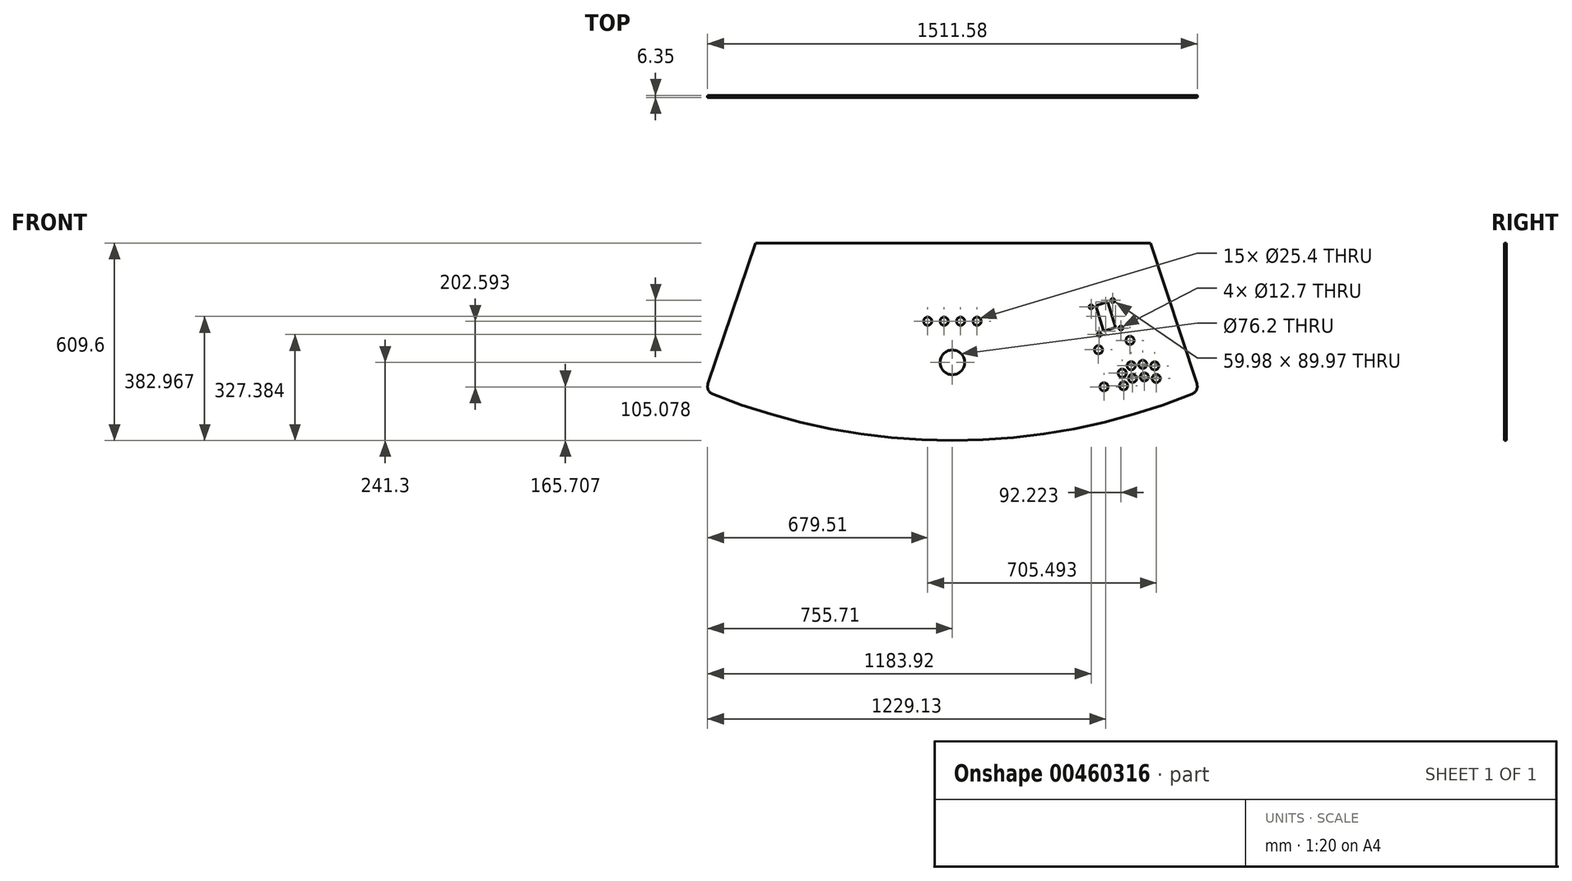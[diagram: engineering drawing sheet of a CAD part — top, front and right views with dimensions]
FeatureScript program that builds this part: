
annotation { "Feature Type Name" : "Feature", "Feature Type Description" : "" }
export const myFeature = defineFeature(function(context is Context, id is Id, definition is map)
    precondition{}
    {
        {
            var Q0;
            Q0=qCreatedBy(makeId("Front.planeOp"),FACE);
            var sketch = newSketch(context, id + "F0", { "sketchPlane" : qUnion([Q0])});
            skLineSegment(sketch, "E0.bottom", {"start": v(-607.8, 0) * mm, "end": v(611.4, 0) * mm});
            skLineSegment(sketch, "E1", {"start": v(-607.8, 0) * mm, "end": v(-754.38, -434.61) * mm});
            skLineSegment(sketch, "E2", {"start": v(611.4, 0) * mm, "end": v(754.6, -434.72) * mm});
            skArc(sketch, "E3", {"start": v(-739.8, -466.3) * mm, "mid": v(0.09, -609.6) * mm, "end": v(739.96, -466.23) * mm});
            skPoint(sketch, "E4.visualSharp", {"position": v(-762, -457.2) * mm});
            skArc(sketch, "E4.filletArc", {"start": v(-754.38, -434.61) * mm, "mid": v(-753.39, -453.35) * mm, "end": v(-739.8, -466.3) * mm});
            skPoint(sketch, "E5.visualSharp", {"position": v(762, -457.2) * mm});
            skArc(sketch, "E5.filletArc", {"start": v(739.96, -466.23) * mm, "mid": v(753.5, -453.37) * mm, "end": v(754.6, -434.72) * mm});
            skSolve(sketch);
        }
        {
            var Q0;
            Q0=qSketchRegion(id+"F0",true);
            extrude(context, id + "F1", {"entities" : qUnion([Q0]), "depth" : 6.35 * mm});
        }
        {
            var Q0;
            Q0=makeQuery(id+"F1.opExtrude","CAP_FACE",FACE,{"disambiguationData":[OSD([sQuery(id+"F0.wireOp",EDGE,"E0.bottom"),sQuery(id+"F0.wireOp",EDGE,"E1"),sQuery(id+"F0.wireOp",EDGE,"E2"),sQuery(id+"F0.wireOp",EDGE,"E3"),sQuery(id+"F0.wireOp",EDGE,"E4.filletArc"),sQuery(id+"F0.wireOp",EDGE,"E5.filletArc")])],"isStart":false});
            var sketch = newSketch(context, id + "F2", { "sketchPlane" : qUnion([Q0])});
            skCircle(sketch, "E6", {"center": v(0, 1371.6) * mm, "radius": 1981.2 * mm, "construction": true});
            skLineSegment(sketch, "E7", {"start": v(0, 1371.6) * mm, "end": v(-562.7, -528.01) * mm, "construction": true});
            skLineSegment(sketch, "E8", {"start": v(0, 1371.6) * mm, "end": v(-189.89, -600.48) * mm, "construction": true});
            skLineSegment(sketch, "E9", {"start": v(0, 1371.6) * mm, "end": v(189.89, -600.48) * mm, "construction": true});
            skLineSegment(sketch, "E10", {"start": v(0, 1371.6) * mm, "end": v(562.7, -528.01) * mm, "construction": true});
            skLineSegment(sketch, "E11", {"start": v(0, 1371.6) * mm, "end": v(-762, -457.2) * mm, "construction": true});
            skLineSegment(sketch, "E12", {"start": v(0, 1371.6) * mm, "end": v(762, -457.2) * mm, "construction": true});
            skLineSegment(sketch, "E13", {"start": v(0, 1371.6) * mm, "end": v(0, -609.6) * mm, "construction": true});
            skLineSegment(sketch, "E14.bottom", {"start": v(422.55, -417.2) * mm, "end": v(618.63, -359.12) * mm, "construction": true});
            skLineSegment(sketch, "E14.top", {"start": v(442.39, -484.18) * mm, "end": v(638.47, -426.1) * mm, "construction": true});
            skLineSegment(sketch, "E14.left", {"start": v(422.55, -417.2) * mm, "end": v(442.39, -484.18) * mm, "construction": true});
            skLineSegment(sketch, "E14.right", {"start": v(618.63, -359.12) * mm, "end": v(638.47, -426.1) * mm, "construction": true});
            skCircle(sketch, "E15", {"center": v(624.6, -379.26) * mm, "radius": 12.7 * mm});
            skCircle(sketch, "E16", {"center": v(629.3, -418.02) * mm, "radius": 12.7 * mm});
            skCircle(sketch, "E17", {"center": v(587.73, -374.53) * mm, "radius": 12.7 * mm});
            skCircle(sketch, "E18", {"center": v(592.43, -413.3) * mm, "radius": 12.7 * mm});
            skCircle(sketch, "E19", {"center": v(551.99, -378.86) * mm, "radius": 12.7 * mm});
            skCircle(sketch, "E20", {"center": v(556.21, -417.76) * mm, "radius": 12.7 * mm});
            skCircle(sketch, "E21", {"center": v(524.32, -401.66) * mm, "radius": 12.7 * mm});
            skCircle(sketch, "E22", {"center": v(528.55, -440.56) * mm, "radius": 12.7 * mm});
            skCircle(sketch, "E23", {"center": v(468, -443.9) * mm, "radius": 12.7 * mm});
            skCircle(sketch, "E24", {"center": v(450.86, -329.34) * mm, "radius": 12.7 * mm});
            skCircle(sketch, "E25", {"center": v(548.28, -300.49) * mm, "radius": 12.7 * mm});
            skLineSegment(sketch, "E26", {"start": v(443.43, -192.47) * mm, "end": v(479.96, -181.65) * mm});
            skLineSegment(sketch, "E27", {"start": v(479.96, -181.65) * mm, "end": v(503.4, -260.8) * mm});
            skLineSegment(sketch, "E28", {"start": v(503.4, -260.8) * mm, "end": v(466.88, -271.62) * mm});
            skLineSegment(sketch, "E29", {"start": v(466.88, -271.62) * mm, "end": v(443.43, -192.47) * mm});
            skCircle(sketch, "E30", {"center": v(453.46, -282.22) * mm, "radius": 6.35 * mm});
            skCircle(sketch, "E31", {"center": v(520.43, -262.38) * mm, "radius": 6.35 * mm});
            skCircle(sketch, "E32", {"center": v(428.2, -196.98) * mm, "radius": 6.35 * mm});
            skCircle(sketch, "E33", {"center": v(495.18, -177.14) * mm, "radius": 6.35 * mm});
            skSolve(sketch);
        }
        {
            var Q0;
            Q0=qSketchRegion(id+"F2",true);
            extrude(context, id + "F3", {"entities" : qUnion([Q0]), "operationType" : NewBodyOperationType.REMOVE, "endBound" : BoundingType.THROUGH_ALL, "oppositeDirection" : true, "depth" : 25.4 * mm});
        }
        {
            var Q0;
            Q0=qCreatedBy(makeId("Top.planeOp"),FACE);
            cPlane(context, id + "F4", {"entities" : qUnion([Q0]), "cplaneType" : CPlaneType.OFFSET, "offset" : 1371.6 * mm, "width" : 152.4 * mm, "height" : 152.4 * mm});
        }
        {
            var Q0;
            Q0=qCreatedBy(id+"F4.planeOp",FACE);
            var sketch = newSketch(context, id + "F5", { "sketchPlane" : qUnion([Q0])});
            skLineSegment(sketch, "E34", {"start": v(0.09, -217.76) * mm, "end": v(0.09, 314.08) * mm, "construction": true});
            skSolve(sketch);
        }
        {
            var Q0;
            Q0=makeQuery(id+"F1.opExtrude","CAP_FACE",FACE,{"disambiguationData":[OSD([sQuery(id+"F0.wireOp",EDGE,"E0.bottom"),sQuery(id+"F0.wireOp",EDGE,"E1"),sQuery(id+"F0.wireOp",EDGE,"E2"),sQuery(id+"F0.wireOp",EDGE,"E3"),sQuery(id+"F0.wireOp",EDGE,"E4.filletArc"),sQuery(id+"F0.wireOp",EDGE,"E5.filletArc")])],"isStart":false});
            var sketch = newSketch(context, id + "F6", { "sketchPlane" : qUnion([Q0])});
            skLineSegment(sketch, "E35", {"start": v(0, 0) * mm, "end": v(0, -609.6) * mm, "construction": true});
            skCircle(sketch, "E36", {"center": v(0, -368.3) * mm, "radius": 38.1 * mm});
            skLineSegment(sketch, "E37", {"start": v(-99.18, -254) * mm, "end": v(154.82, -254) * mm, "construction": true});
            skCircle(sketch, "E38", {"center": v(-76.2, -241.3) * mm, "radius": 12.7 * mm});
            skCircle(sketch, "E39.1.0.0", {"center": v(-25.4, -241.3) * mm, "radius": 12.7 * mm});
            skCircle(sketch, "E39.2.0.0", {"center": v(25.4, -241.3) * mm, "radius": 12.7 * mm});
            skCircle(sketch, "E39.3.0.0", {"center": v(76.2, -241.3) * mm, "radius": 12.7 * mm});
            skLineSegment(sketch, "E39.direction1", {"start": v(-76.2, -241.3) * mm, "end": v(-25.4, -241.3) * mm, "construction": true});
            skSolve(sketch);
        }
        {
            var Q0;
            Q0=qSketchRegion(id+"F6",true);
            extrude(context, id + "F7", {"entities" : qUnion([Q0]), "operationType" : NewBodyOperationType.REMOVE, "endBound" : BoundingType.THROUGH_ALL, "oppositeDirection" : true, "depth" : 25.4 * mm});
        }
    });
